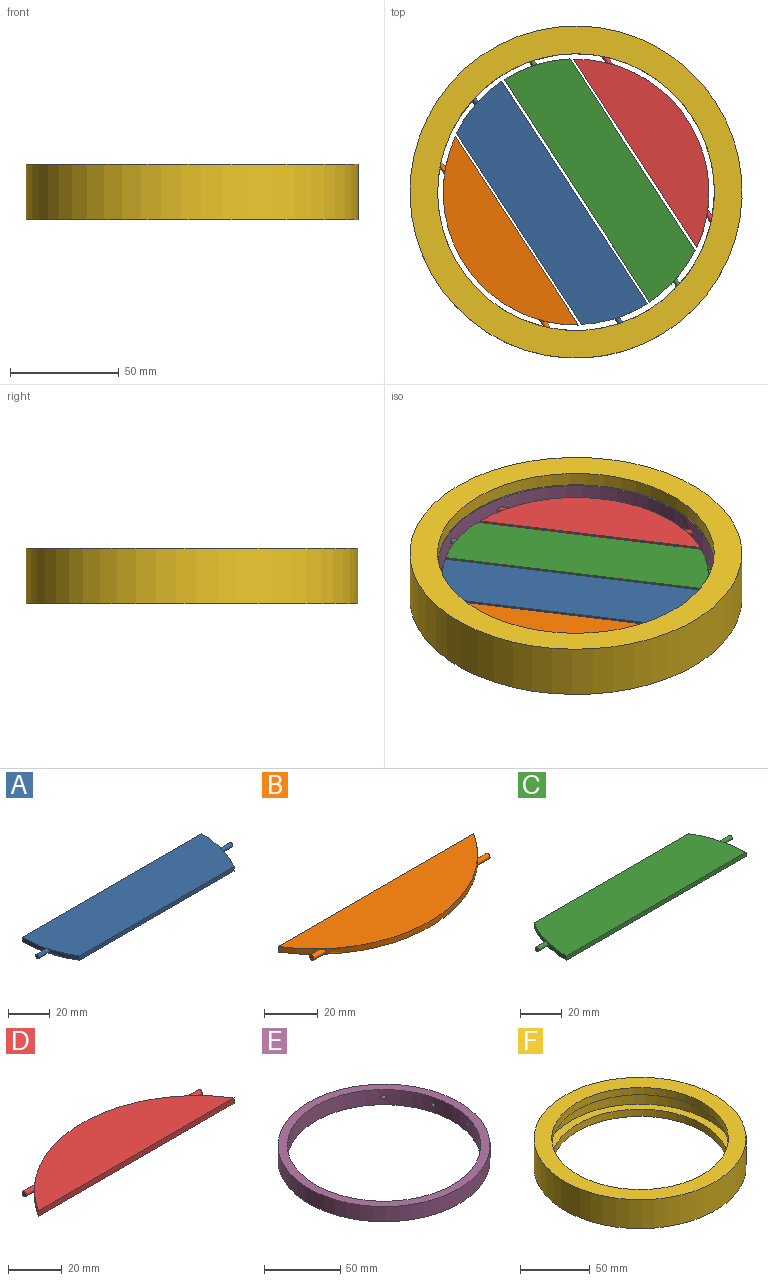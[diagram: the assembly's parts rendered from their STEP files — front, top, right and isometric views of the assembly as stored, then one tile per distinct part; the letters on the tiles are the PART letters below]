
ASSEMBLY  parts=6 mates=5
PART A: 10 faces, bbox 131.6x30.5x2.5 mm
  f0: cylinder r=1.14mm len=7.25mm, axis (-1,0,0), area 49.8mm2, adj f1,f2
  f1: plane 2.29x2.29mm, normal (-1,0,0), area 4.1mm2, adj f0
  f2: cylinder r=60.96mm len=30.48mm, axis (0,0,-1), area 77.1mm2, adj f0,f4,f5,f6,f7
  f3: cylinder r=60.96mm len=30.48mm, axis (0,0,-1), area 77.1mm2, adj f4,f5,f6,f7,f9
  f4: plane 121.91x2.54mm, normal (0,1,0), area 309.7mm2, adj f2,f3,f6,f7
  f5: plane 104.84x2.54mm, normal (0,-1,0), area 266.3mm2, adj f2,f3,f6,f7
  f6: plane 121.91x30.48mm, normal (0,0,1), area 3544.3mm2, adj f2,f3,f4,f5
  f7: plane 121.91x30.48mm, normal (0,0,-1), area 3544.3mm2, adj f2,f3,f4,f5
  f8: plane 2.29x2.29mm, normal (1,0,0), area 4.1mm2, adj f9
  f9: cylinder r=1.14mm len=7.25mm, axis (-1,0,0), area 49.8mm2, adj f3,f8
PART B: 8 faces, bbox 103.3x28.6x2.5 mm
  f0: cylinder r=1.14mm len=6.74mm, axis (-1,0,0), area 39.3mm2, adj f1,f2
  f1: plane 2.29x2.29mm, normal (1,0,0), area 4.1mm2, adj f0
  f2: cylinder r=60.96mm len=103.29mm, axis (0,0,-1), area 301mm2, adj f0,f3,f4,f5,f7
  f3: plane 103.29x2.54mm, normal (0,1,0), area 262.4mm2, adj f2,f4,f5
  f4: plane 103.29x28.58mm, normal (0,0,1), area 2083.4mm2, adj f2,f3
  f5: plane 103.29x28.58mm, normal (0,0,-1), area 2083.4mm2, adj f2,f3
  f6: plane 2.29x2.29mm, normal (-1,0,0), area 4.1mm2, adj f7
  f7: cylinder r=1.14mm len=6.74mm, axis (-1,0,0), area 39.3mm2, adj f2,f6
PART C: 10 faces, bbox 131.6x30.5x2.5 mm
  f0: cylinder r=1.14mm len=7.25mm, axis (-1,0,0), area 49.8mm2, adj f1,f2
  f1: plane 2.29x2.29mm, normal (-1,0,0), area 4.1mm2, adj f0
  f2: cylinder r=60.96mm len=30.48mm, axis (0,0,-1), area 77.1mm2, adj f0,f4,f5,f6,f7
  f3: cylinder r=60.96mm len=30.48mm, axis (0,0,-1), area 77.1mm2, adj f4,f5,f6,f7,f9
  f4: plane 121.91x2.54mm, normal (0,-1,0), area 309.7mm2, adj f2,f3,f6,f7
  f5: plane 104.84x2.54mm, normal (0,1,0), area 266.3mm2, adj f2,f3,f6,f7
  f6: plane 121.91x30.48mm, normal (0,0,1), area 3544.3mm2, adj f2,f3,f4,f5
  f7: plane 121.91x30.48mm, normal (0,0,-1), area 3544.3mm2, adj f2,f3,f4,f5
  f8: plane 2.29x2.29mm, normal (1,0,0), area 4.1mm2, adj f9
  f9: cylinder r=1.14mm len=7.25mm, axis (-1,0,0), area 49.8mm2, adj f3,f8
PART D: 8 faces, bbox 103.3x28.6x2.5 mm
  f0: cylinder r=1.14mm len=6.74mm, axis (-1,0,0), area 39.3mm2, adj f1,f2
  f1: plane 2.29x2.29mm, normal (1,0,0), area 4.1mm2, adj f0
  f2: cylinder r=60.96mm len=103.29mm, axis (0,0,-1), area 301mm2, adj f0,f3,f4,f5,f7
  f3: plane 103.29x2.54mm, normal (0,-1,0), area 262.4mm2, adj f2,f4,f5
  f4: plane 103.29x28.58mm, normal (0,0,1), area 2083.4mm2, adj f2,f3
  f5: plane 103.29x28.58mm, normal (0,0,-1), area 2083.4mm2, adj f2,f3
  f6: plane 2.29x2.29mm, normal (-1,0,0), area 4.1mm2, adj f7
  f7: cylinder r=1.14mm len=6.74mm, axis (-1,0,0), area 39.3mm2, adj f2,f6
PART E: 20 faces, bbox 139.2x139.2x12.2 mm
  f0: cylinder r=63.5mm len=127mm, axis (0,0,1), area 4814.6mm2, adj f1,f3,f5,f6,f9,f10,f13,f14
  f1: plane 139.19x139.19mm, normal (0,0,1), area 2548.9mm2, adj f0,f2
  f2: cylinder r=69.6mm len=139.19mm, axis (0,0,1), area 5331.4mm2, adj f1,f3
  f3: plane 139.19x139.19mm, normal (0,0,-1), area 2548.9mm2, adj f0,f2
  f4: plane 2.54x2.54mm, normal (-1,0,0), area 5.1mm2, adj f5
  f5: cylinder r=1.27mm len=4.9mm, axis (1,0,0), area 36.4mm2, adj f0,f4
  f6: cylinder r=1.27mm len=4.9mm, axis (1,0,0), area 36.4mm2, adj f0,f7
  f7: plane 2.54x2.54mm, normal (1,0,0), area 5.1mm2, adj f6
  f8: plane 2.54x2.54mm, normal (-1,0,0), area 5.1mm2, adj f9
  f9: cylinder r=1.27mm len=4.9mm, axis (1,0,0), area 36.4mm2, adj f0,f8
  f10: cylinder r=1.27mm len=4.9mm, axis (1,0,0), area 36.4mm2, adj f0,f11
  f11: plane 2.54x2.54mm, normal (1,0,0), area 5.1mm2, adj f10
  f12: plane 2.54x2.54mm, normal (-1,0,0), area 5.1mm2, adj f13
  f13: cylinder r=1.27mm len=6.13mm, axis (1,0,0), area 38.6mm2, adj f0,f12
  f14: cylinder r=1.27mm len=6.13mm, axis (1,0,0), area 38.5mm2, adj f0,f15
  f15: plane 2.54x2.54mm, normal (1,0,0), area 5.1mm2, adj f14
  f16: plane 2.54x2.54mm, normal (-1,0,0), area 5.1mm2, adj f17
  f17: cylinder r=1.27mm len=6.13mm, axis (1,0,0), area 38.5mm2, adj f0,f16
  f18: cylinder r=1.27mm len=6.13mm, axis (1,0,0), area 38.6mm2, adj f0,f19
  f19: plane 2.54x2.54mm, normal (1,0,0), area 5.1mm2, adj f18
PART F: 8 faces, bbox 152.4x152.4x25.4 mm
  f0: cylinder r=76.2mm len=152.4mm, axis (0,0,1), area 12161mm2, adj f1,f7
  f1: plane 152.4x152.4mm, normal (0,0,-1), area 5573.8mm2, adj f0,f2
  f2: cylinder r=63.5mm len=127mm, axis (0,0,1), area 2533.5mm2, adj f1,f3
  f3: plane 139.7x139.7mm, normal (0,0,1), area 2660.2mm2, adj f2,f4
  f4: cylinder r=69.85mm len=139.7mm, axis (0,0,1), area 5573.8mm2, adj f3,f5
  f5: plane 139.7x139.7mm, normal (0,0,-1), area 2660.2mm2, adj f4,f6
  f6: cylinder r=63.5mm len=127mm, axis (0,0,1), area 2533.5mm2, adj f5,f7
  f7: plane 152.4x152.4mm, normal (0,0,1), area 5573.8mm2, adj f0,f6
PLACE A rot(axis=(-0.48,-0.88,0),180deg) t=(-0.14,0.21,0)mm
PLACE B rot(axis=(0,0,-1),56.8deg) t=(0.02,-0.03,0)mm
PLACE C rot(axis=(-0.48,-0.88,0),180deg) t=(-0.14,0.21,0)mm
PLACE D rot(axis=(-0.48,-0.88,0),180deg) t=(0.02,-0.03,0)mm
PLACE E rot(axis=(0,0,-1),56.8deg) t=(0,0,0)mm
PLACE F rot(axis=(0,0,1),33.2deg) t=(0,0,0.25)mm
MATE revolute A.f0 <-> E.f9  axis (-0.55,0.84,0) through (-49.44,46.58,0)mm
MATE revolute D.f0 <-> E.f13  axis (-0.55,0.84,0) through (12.31,63.55,0)mm
MATE fastened F.f0 <-> E.f0  axis (0,0,1) through (0,0,-6.1)mm
MATE revolute B.f0 <-> E.f17  axis (-0.55,0.84,0) through (-63.15,14.19,0)mm
MATE revolute C.f0 <-> E.f5  axis (0.55,-0.84,0) through (-22.87,63.96,0)mm
